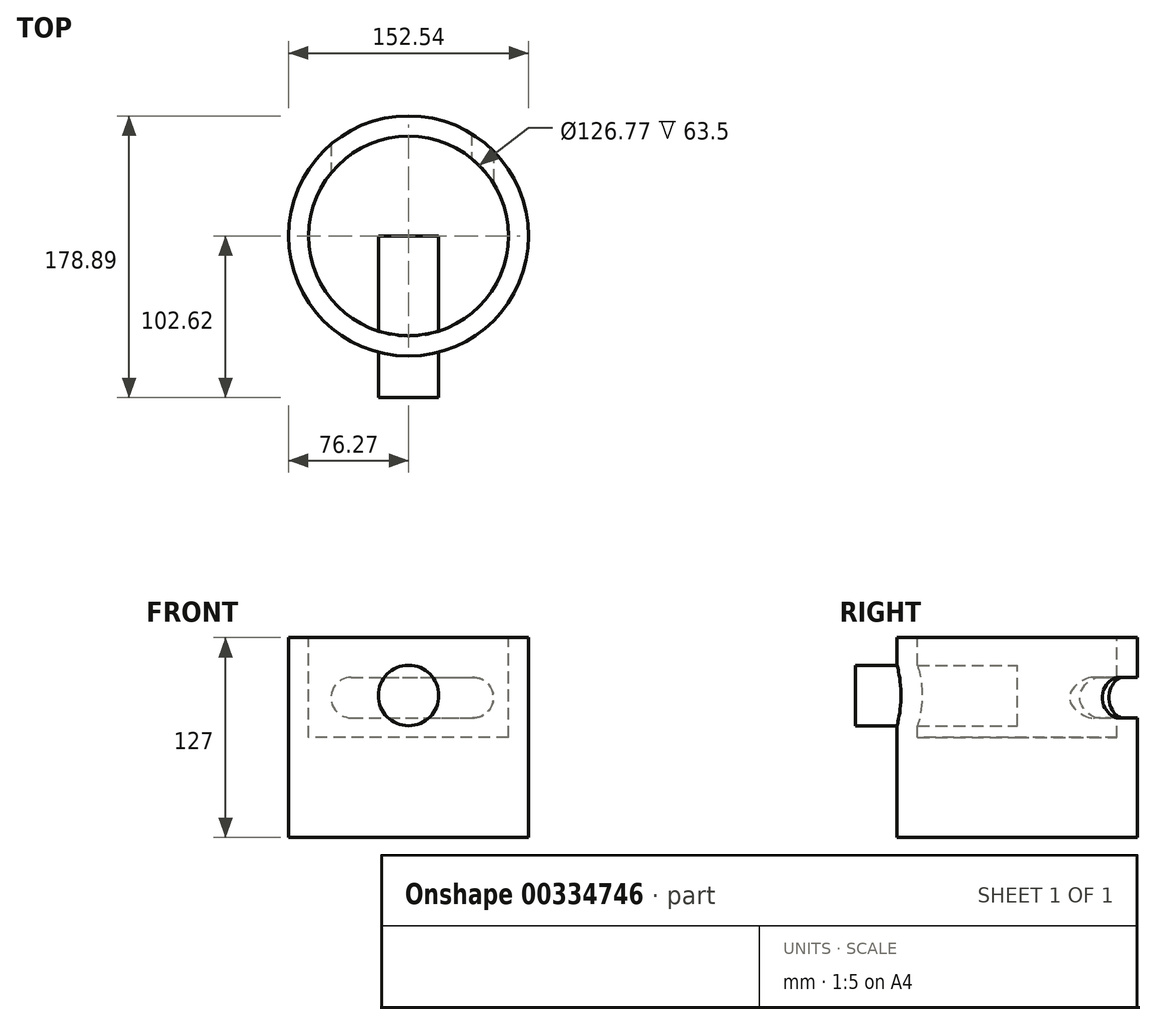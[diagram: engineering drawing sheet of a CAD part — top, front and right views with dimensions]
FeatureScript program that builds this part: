
annotation { "Feature Type Name" : "Feature", "Feature Type Description" : "" }
export const myFeature = defineFeature(function(context is Context, id is Id, definition is map)
    precondition{}
    {
        {
            var Q0;
            Q0=qCreatedBy(makeId("Top.planeOp"),FACE);
            var sketch = newSketch(context, id + "F0", { "sketchPlane" : qUnion([Q0])});
            skCircle(sketch, "E0", {"center": v(0, 0) * mm, "radius": 76.27 * mm});
            skSolve(sketch);
        }
        {
            var Q0;
            Q0 = qSketchRegion(id + "F0", true);
            extrude(context, id + "F1", {"entities" : qUnion([Q0]), "depth" : 127 * mm});
        }
        {
            var Q0;
            Q0=makeQuery(id+"F1.opExtrude","CAP_FACE",FACE,{"disambiguationData":[OSD([sQuery(id+"F0.wireOp",EDGE,"E0")])],"isStart":false});
            var sketch = newSketch(context, id + "F2", { "sketchPlane" : qUnion([Q0])});
            skCircle(sketch, "E1", {"center": v(0, 0) * mm, "radius": 63.38 * mm});
            skSolve(sketch);
        }
        {
            var Q0;
            Q0 = qSketchRegion(id + "F2", true);
            extrude(context, id + "F3", {"entities" : qUnion([Q0]), "operationType" : NewBodyOperationType.REMOVE, "oppositeDirection" : true, "depth" : 63.5 * mm});
        }
        {
            var Q0;
            Q0=qCreatedBy(makeId("Front.planeOp"),FACE);
            var sketch = newSketch(context, id + "F4", { "sketchPlane" : qUnion([Q0])});
            skLineSegment(sketch, "E2.bottom", {"start": v(-36.46, 76.05) * mm, "end": v(41.06, 76.05) * mm});
            skLineSegment(sketch, "E2.top", {"start": v(-36.46, 101.76) * mm, "end": v(41.06, 101.76) * mm});
            skLineSegment(sketch, "E2.left", {"start": v(-36.46, 76.05) * mm, "end": v(-36.46, 101.76) * mm});
            skLineSegment(sketch, "E2.right", {"start": v(41.06, 76.05) * mm, "end": v(41.06, 101.76) * mm});
            skCircle(sketch, "E3", {"center": v(41.06, 88.9) * mm, "radius": 12.9 * mm});
            skCircle(sketch, "E4", {"center": v(-36.46, 88.9) * mm, "radius": 12.86 * mm});
            skSolve(sketch);
        }
        {
            var Q0;
            Q0 = qSketchRegion(id + "F4", true);
            extrude(context, id + "F5", {"entities" : qUnion([Q0]), "operationType" : NewBodyOperationType.REMOVE, "oppositeDirection" : true, "depth" : 127 * mm});
        }
        {
            var Q0;
            Q0=qCreatedBy(makeId("Front.planeOp"),FACE);
            var sketch = newSketch(context, id + "F6", { "sketchPlane" : qUnion([Q0])});
            skLineSegment(sketch, "E5.bottom", {"start": v(0, 0) * mm, "end": v(75.98, 0) * mm, "construction": true});
            skLineSegment(sketch, "E5.top", {"start": v(0, 90.25) * mm, "end": v(75.98, 90.25) * mm, "construction": true});
            skLineSegment(sketch, "E5.left", {"start": v(0, 0) * mm, "end": v(0, 90.25) * mm, "construction": true});
            skLineSegment(sketch, "E5.right", {"start": v(75.98, 0) * mm, "end": v(75.98, 90.25) * mm, "construction": true});
            skCircle(sketch, "E6", {"center": v(0, 90.25) * mm, "radius": 19.2 * mm});
            skSolve(sketch);
        }
        {
            var Q0;
            Q0 = qSketchRegion(id + "F6", true);
            extrude(context, id + "F7", {"entities" : qUnion([Q0]), "operationType" : NewBodyOperationType.ADD, "depth" : 102.62 * mm});
        }
    });
